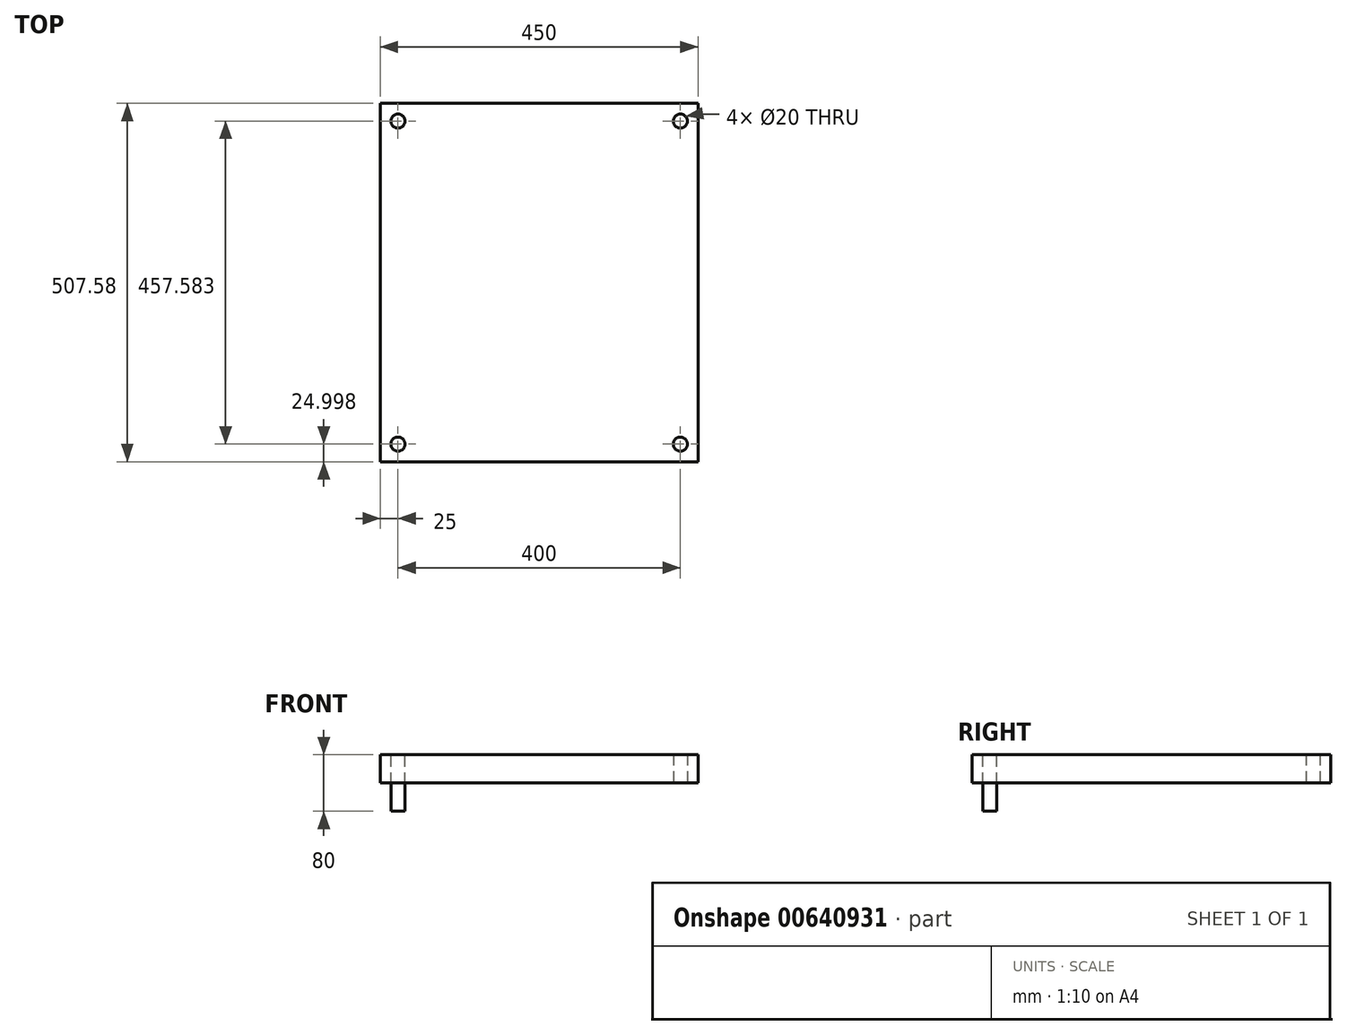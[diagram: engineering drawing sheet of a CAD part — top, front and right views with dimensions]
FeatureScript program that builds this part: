
annotation { "Feature Type Name" : "Feature", "Feature Type Description" : "" }
export const myFeature = defineFeature(function(context is Context, id is Id, definition is map)
    precondition{}
    {
        {
            var Q0;
            Q0=qCreatedBy(makeId("Top.planeOp"),FACE);
            var sketch = newSketch(context, id + "F0", { "sketchPlane" : qUnion([Q0])});
            skLineSegment(sketch, "E0.bottom", {"start": v(225, -253.8) * mm, "end": v(-225, -253.8) * mm});
            skLineSegment(sketch, "E0.top", {"start": v(225, 253.8) * mm, "end": v(-225, 253.8) * mm});
            skLineSegment(sketch, "E0.left", {"start": v(225, -253.8) * mm, "end": v(225, 253.8) * mm});
            skLineSegment(sketch, "E0.right", {"start": v(-225, -253.8) * mm, "end": v(-225, 253.8) * mm});
            skPoint(sketch, "E0.middle", {"position": v(0, 0) * mm});
            skCircle(sketch, "E1", {"center": v(-200, 228.8) * mm, "radius": 10 * mm});
            skCircle(sketch, "E2", {"center": v(200, 228.8) * mm, "radius": 10 * mm});
            skCircle(sketch, "E3", {"center": v(200, -228.8) * mm, "radius": 10 * mm});
            skCircle(sketch, "E4", {"center": v(-200, -228.8) * mm, "radius": 10 * mm});
            skSolve(sketch);
        }
        {
            var Q0;
            Q0=makeQuery(id+"F0.imprint","IMPRINT",FACE,{"disambiguationData":[TD([[makeQuery(id+"F0.imprint","IMPRINT",EDGE,{"derivedFrom":sQuery(id+"F0.wireOp",EDGE,"E0.bottom")}),-1.0]])]});
            extrude(context, id + "F1", {"entities" : qUnion([Q0]), "depth" : 40 * mm, "offsetDistance" : 25 * mm});
        }
        {
            var Q0;
            Q0=makeQuery(id+"F1.opExtrude","CAP_FACE",FACE,{"disambiguationData":[OSD([sQuery(id+"F0.wireOp",EDGE,"E0.bottom"),sQuery(id+"F0.wireOp",EDGE,"E0.top"),sQuery(id+"F0.wireOp",EDGE,"E0.left"),sQuery(id+"F0.wireOp",EDGE,"E0.right"),sQuery(id+"F0.wireOp",EDGE,"E1"),sQuery(id+"F0.wireOp",EDGE,"E2"),sQuery(id+"F0.wireOp",EDGE,"E3"),sQuery(id+"F0.wireOp",EDGE,"E4")])],"isStart":false});
            var sketch = newSketch(context, id + "F2", { "sketchPlane" : qUnion([Q0])});
            skCircle(sketch, "E5.0", {"center": v(-200, -228.8) * mm, "radius": 10 * mm});
            skSolve(sketch);
        }
        {
            var Q0;
            Q0=makeQuery(id+"F2.imprint","IMPRINT",FACE,{"disambiguationData":[TD([[makeQuery(id+"F2.imprint","IMPRINT",EDGE,{"derivedFrom":sQuery(id+"F2.wireOp",EDGE,"E5.0")}),1.0]])]});
            extrude(context, id + "F3", {"entities" : qUnion([Q0]), "depth" : -80 * mm, "offsetDistance" : 25 * mm});
        }
        {
            var Q0;
            Q0=makeQuery(id+"F1.opExtrude","CAP_FACE",FACE,{"disambiguationData":[OSD([sQuery(id+"F0.wireOp",EDGE,"E0.bottom"),sQuery(id+"F0.wireOp",EDGE,"E0.top"),sQuery(id+"F0.wireOp",EDGE,"E0.left"),sQuery(id+"F0.wireOp",EDGE,"E0.right"),sQuery(id+"F0.wireOp",EDGE,"E1"),sQuery(id+"F0.wireOp",EDGE,"E2"),sQuery(id+"F0.wireOp",EDGE,"E3"),sQuery(id+"F0.wireOp",EDGE,"E4")])],"isStart":true});
            var sketch = newSketch(context, id + "F4", { "sketchPlane" : qUnion([Q0])});
            skCircle(sketch, "E6", {"center": v(-200, 228.8) * mm, "radius": 25 * mm});
            skSolve(sketch);
        }
        {
            var Q0;
            Q0=sQuery(id+"F4.wireOp",EDGE,"E6");
            extrude(context, id + "F5", {"bodyType" : ToolBodyType.SURFACE, "surfaceEntities" : qUnion([Q0]), "depth" : 420 * mm, "offsetDistance" : 25 * mm});
        }
    });
